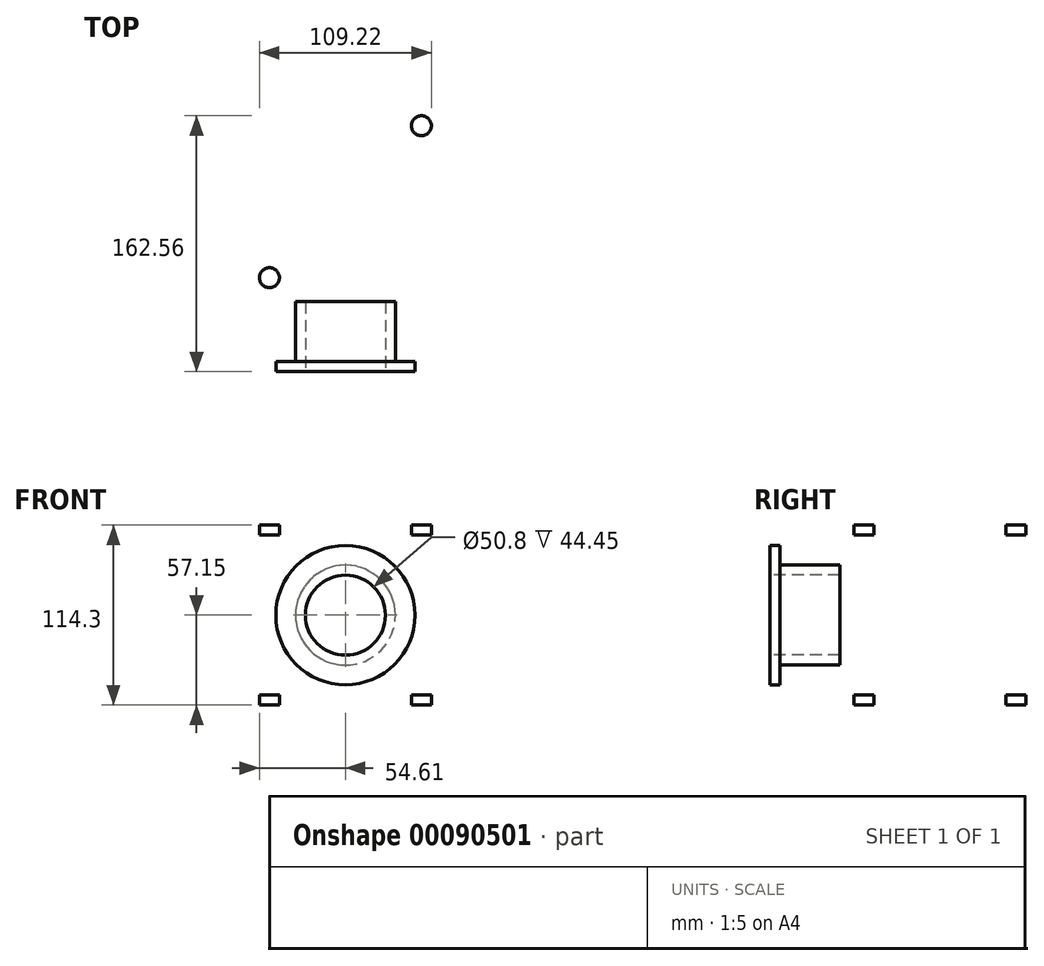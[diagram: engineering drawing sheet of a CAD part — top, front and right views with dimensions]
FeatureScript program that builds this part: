
annotation { "Feature Type Name" : "Feature", "Feature Type Description" : "" }
export const myFeature = defineFeature(function(context is Context, id is Id, definition is map)
    precondition{}
    {
        {
            var Q0;
            Q0=qCreatedBy(makeId("Top.planeOp"),FACE);
            var sketch = newSketch(context, id + "F0", { "sketchPlane" : qUnion([Q0])});
            skLineSegment(sketch, "E0", {"start": v(0, 63.5) * mm, "end": v(63.5, 63.5) * mm});
            skLineSegment(sketch, "E1", {"start": v(63.5, 63.5) * mm, "end": v(63.5, 0) * mm});
            skLineSegment(sketch, "E2.MirrorCS", {"start": v(-63.5, 63.5) * mm, "end": v(-63.5, 0) * mm});
            skLineSegment(sketch, "E3.MirrorCS", {"start": v(0, 63.5) * mm, "end": v(-63.5, 63.5) * mm});
            skLineSegment(sketch, "E4.MirrorCS", {"start": v(-63.5, -63.5) * mm, "end": v(-63.5, 0) * mm});
            skLineSegment(sketch, "E5.MirrorCS", {"start": v(0, -63.5) * mm, "end": v(-63.5, -63.5) * mm});
            skLineSegment(sketch, "E6.MirrorCS", {"start": v(0, -63.5) * mm, "end": v(63.5, -63.5) * mm});
            skLineSegment(sketch, "E7.MirrorCS", {"start": v(63.5, -63.5) * mm, "end": v(63.5, 0) * mm});
            skSolve(sketch);
        }
        {
            var Q0;
            Q0 = qSketchRegion(id + "F0", true);
            extrude(context, id + "F1", {"entities" : qUnion([Q0]), "depth" : 6.35 * mm});
        }
        {
            var Q0;
            Q0=makeQuery(id+"F1.opExtrude","SWEPT_EDGE",EDGE,{"disambiguationData":[OSD([sQuery(id+"F0.wireOp",EDGE,"E6.MirrorCS"),sQuery(id+"F0.wireOp",EDGE,"E7.MirrorCS")])]});
            var Q1;
            Q1=makeQuery(id+"F1.opExtrude","SWEPT_EDGE",EDGE,{"disambiguationData":[OSD([sQuery(id+"F0.wireOp",EDGE,"E0"),sQuery(id+"F0.wireOp",EDGE,"E1")])]});
            var Q2;
            Q2=makeQuery(id+"F1.opExtrude","SWEPT_EDGE",EDGE,{"disambiguationData":[OSD([sQuery(id+"F0.wireOp",EDGE,"E4.MirrorCS"),sQuery(id+"F0.wireOp",EDGE,"E5.MirrorCS")])]});
            var Q3;
            Q3=makeQuery(id+"F1.opExtrude","SWEPT_EDGE",EDGE,{"disambiguationData":[OSD([sQuery(id+"F0.wireOp",EDGE,"E2.MirrorCS"),sQuery(id+"F0.wireOp",EDGE,"E3.MirrorCS")])]});
            fillet(context, id + "F2", {"entities" : qUnion([Q0, Q1, Q2, Q3]), "radius" : 25.4 * mm, "tangentPropagation" : true, "allowEdgeOverflow" : false});
        }
        {
            var Q0;
            Q0=makeQuery(id+"F1.opExtrude","CAP_FACE",FACE,{"disambiguationData":[OSD([sQuery(id+"F0.wireOp",EDGE,"E0"),sQuery(id+"F0.wireOp",EDGE,"E1"),sQuery(id+"F0.wireOp",EDGE,"E2.MirrorCS"),sQuery(id+"F0.wireOp",EDGE,"E3.MirrorCS"),sQuery(id+"F0.wireOp",EDGE,"E4.MirrorCS"),sQuery(id+"F0.wireOp",EDGE,"E5.MirrorCS"),sQuery(id+"F0.wireOp",EDGE,"E6.MirrorCS"),sQuery(id+"F0.wireOp",EDGE,"E7.MirrorCS")])],"isStart":false});
            var sketch = newSketch(context, id + "F3", { "sketchPlane" : qUnion([Q0])});
            skCircle(sketch, "E8", {"center": v(0, 0) * mm, "radius": 47.63 * mm});
            skSolve(sketch);
        }
        {
            var Q0;
            Q0 = qSketchRegion(id + "F3", true);
            extrude(context, id + "F4", {"entities" : qUnion([Q0]), "operationType" : NewBodyOperationType.ADD, "depth" : 101.6 * mm});
        }
        {
            var Q0;
            Q0=makeQuery(id+"F4.opExtrude","CAP_FACE",FACE,{"disambiguationData":[OSD([sQuery(id+"F3.wireOp",EDGE,"E8")])],"isStart":false});
            var sketch = newSketch(context, id + "F5", { "sketchPlane" : qUnion([Q0])});
            skLineSegment(sketch, "E9", {"start": v(0, 63.5) * mm, "end": v(63.5, 63.5) * mm});
            skLineSegment(sketch, "E10", {"start": v(63.5, 63.5) * mm, "end": v(63.5, 0) * mm});
            skLineSegment(sketch, "E11.MirrorCS", {"start": v(0, 63.5) * mm, "end": v(-63.5, 63.5) * mm});
            skLineSegment(sketch, "E12.MirrorCS", {"start": v(-63.5, 63.5) * mm, "end": v(-63.5, 0) * mm});
            skLineSegment(sketch, "E13.MirrorCS", {"start": v(-63.5, -63.5) * mm, "end": v(-63.5, 0) * mm});
            skLineSegment(sketch, "E14.MirrorCS", {"start": v(0, -63.5) * mm, "end": v(-63.5, -63.5) * mm});
            skLineSegment(sketch, "E15.MirrorCS", {"start": v(0, -63.5) * mm, "end": v(63.5, -63.5) * mm});
            skLineSegment(sketch, "E16.MirrorCS", {"start": v(63.5, -63.5) * mm, "end": v(63.5, 0) * mm});
            skSolve(sketch);
        }
        {
            var Q0;
            Q0 = qSketchRegion(id + "F5", true);
            extrude(context, id + "F6", {"entities" : qUnion([Q0]), "operationType" : NewBodyOperationType.ADD, "depth" : 6.35 * mm});
        }
        {
            var Q0;
            Q0=makeQuery(id+"F6.opExtrude","SWEPT_EDGE",EDGE,{"disambiguationData":[OSD([sQuery(id+"F5.wireOp",EDGE,"E15.MirrorCS"),sQuery(id+"F5.wireOp",EDGE,"E16.MirrorCS")])]});
            var Q1;
            Q1=makeQuery(id+"F6.opExtrude","SWEPT_EDGE",EDGE,{"disambiguationData":[OSD([sQuery(id+"F5.wireOp",EDGE,"E13.MirrorCS"),sQuery(id+"F5.wireOp",EDGE,"E14.MirrorCS")])]});
            var Q2;
            Q2=makeQuery(id+"F6.opExtrude","SWEPT_EDGE",EDGE,{"disambiguationData":[OSD([sQuery(id+"F5.wireOp",EDGE,"E9"),sQuery(id+"F5.wireOp",EDGE,"E10")])]});
            var Q3;
            Q3=makeQuery(id+"F6.opExtrude","SWEPT_EDGE",EDGE,{"disambiguationData":[OSD([sQuery(id+"F5.wireOp",EDGE,"E11.MirrorCS"),sQuery(id+"F5.wireOp",EDGE,"E12.MirrorCS")])]});
            fillet(context, id + "F7", {"entities" : qUnion([Q0, Q1, Q2, Q3]), "radius" : 25.4 * mm, "tangentPropagation" : true, "allowEdgeOverflow" : false});
        }
        {
            var Q0;
            Q0=qCreatedBy(makeId("Front.planeOp"),FACE);
            var sketch = newSketch(context, id + "F8", { "sketchPlane" : qUnion([Q0])});
            skCircle(sketch, "E17", {"center": v(0, 57.15) * mm, "radius": 31.75 * mm});
            skSolve(sketch);
        }
        {
            var Q0;
            Q0 = qSketchRegion(id + "F8", true);
            extrude(context, id + "F9", {"entities" : qUnion([Q0]), "operationType" : NewBodyOperationType.ADD, "depth" : 101.6 * mm});
        }
        {
            var Q0;
            Q0=makeQuery(id+"F9.opExtrude","CAP_FACE",FACE,{"disambiguationData":[OSD([sQuery(id+"F8.wireOp",EDGE,"E17")])],"isStart":false});
            var sketch = newSketch(context, id + "F10", { "sketchPlane" : qUnion([Q0])});
            skCircle(sketch, "E18", {"center": v(0, 57.15) * mm, "radius": 44.2 * mm});
            skSolve(sketch);
        }
        {
            var Q0;
            Q0=makeQuery(id+"F10.imprint","IMPRINT",FACE,{"disambiguationData":[TD([[makeQuery(id+"F10.imprint","IMPRINT",EDGE,{"derivedFrom":sQuery(id+"F10.wireOp",EDGE,"E18")}),1.0]])]});
            var Q1;
            Q1=makeQuery(id+"F10.imprint","IMPRINT",FACE,{"disambiguationData":[TD([[makeQuery(id+"F10.imprint","IMPRINT",EDGE,{"derivedFrom":makeQuery(id+"F9.opExtrude","CAP_EDGE",EDGE,{"disambiguationData":[OSD([sQuery(id+"F8.wireOp",EDGE,"E17")])],"isStart":false})}),1.0]])]});
            extrude(context, id + "F11", {"entities" : qUnion([Q0, Q1]), "operationType" : NewBodyOperationType.ADD, "depth" : 6.35 * mm});
        }
        {
            var Q0;
            Q0=makeQuery(id+"F6.opExtrude","CAP_FACE",FACE,{"disambiguationData":[OSD([sQuery(id+"F5.wireOp",EDGE,"E9"),sQuery(id+"F5.wireOp",EDGE,"E10"),sQuery(id+"F5.wireOp",EDGE,"E11.MirrorCS"),sQuery(id+"F5.wireOp",EDGE,"E12.MirrorCS"),sQuery(id+"F5.wireOp",EDGE,"E13.MirrorCS"),sQuery(id+"F5.wireOp",EDGE,"E14.MirrorCS"),sQuery(id+"F5.wireOp",EDGE,"E15.MirrorCS"),sQuery(id+"F5.wireOp",EDGE,"E16.MirrorCS")])],"isStart":false});
            var sketch = newSketch(context, id + "F12", { "sketchPlane" : qUnion([Q0])});
            skCircle(sketch, "E19", {"center": v(0, 0) * mm, "radius": 38.1 * mm});
            skSolve(sketch);
        }
        {
            var Q0;
            Q0 = qSketchRegion(id + "F12", true);
            extrude(context, id + "F13", {"entities" : qUnion([Q0]), "operationType" : NewBodyOperationType.REMOVE, "oppositeDirection" : true, "depth" : 114.3 * mm});
        }
        {
            var Q0;
            Q0=makeQuery(id+"F11.opExtrude","CAP_FACE",FACE,{"disambiguationData":[OSD([sQuery(id+"F10.wireOp",EDGE,"E18")])],"isStart":false});
            var sketch = newSketch(context, id + "F14", { "sketchPlane" : qUnion([Q0])});
            skCircle(sketch, "E20", {"center": v(0, 57.15) * mm, "radius": 25.4 * mm});
            skSolve(sketch);
        }
        {
            var Q0;
            Q0=makeQuery(id+"F14.imprint","IMPRINT",FACE,{"disambiguationData":[TD([[makeQuery(id+"F14.imprint","IMPRINT",EDGE,{"derivedFrom":sQuery(id+"F14.wireOp",EDGE,"E20")}),1.0]])]});
            extrude(context, id + "F15", {"entities" : qUnion([Q0]), "operationType" : NewBodyOperationType.REMOVE, "oppositeDirection" : true, "depth" : 88.9 * mm});
        }
        {
            var Q0;
            Q0=makeQuery(id+"F6.opExtrude","CAP_FACE",FACE,{"disambiguationData":[OSD([sQuery(id+"F5.wireOp",EDGE,"E9"),sQuery(id+"F5.wireOp",EDGE,"E10"),sQuery(id+"F5.wireOp",EDGE,"E11.MirrorCS"),sQuery(id+"F5.wireOp",EDGE,"E12.MirrorCS"),sQuery(id+"F5.wireOp",EDGE,"E13.MirrorCS"),sQuery(id+"F5.wireOp",EDGE,"E14.MirrorCS"),sQuery(id+"F5.wireOp",EDGE,"E15.MirrorCS"),sQuery(id+"F5.wireOp",EDGE,"E16.MirrorCS")])],"isStart":false});
            var sketch = newSketch(context, id + "F16", { "sketchPlane" : qUnion([Q0])});
            skCircle(sketch, "E21", {"center": v(-48.26, 48.26) * mm, "radius": 6.35 * mm});
            skCircle(sketch, "E22.MirrorC", {"center": v(48.26, 48.26) * mm, "radius": 6.35 * mm});
            skCircle(sketch, "E23.MirrorC", {"center": v(-48.26, -48.26) * mm, "radius": 6.35 * mm});
            skCircle(sketch, "E24.MirrorC", {"center": v(48.26, -48.26) * mm, "radius": 6.35 * mm});
            skSolve(sketch);
        }
        {
            var Q0;
            Q0=makeQuery(id+"F16.imprint","IMPRINT",FACE,{"disambiguationData":[TD([[makeQuery(id+"F16.imprint","IMPRINT",EDGE,{"derivedFrom":sQuery(id+"F16.wireOp",EDGE,"E21")}),1.0]])]});
            var Q1;
            Q1=makeQuery(id+"F16.imprint","IMPRINT",FACE,{"disambiguationData":[TD([[makeQuery(id+"F16.imprint","IMPRINT",EDGE,{"derivedFrom":sQuery(id+"F16.wireOp",EDGE,"E22.MirrorC")}),-1.0]])]});
            var Q2;
            Q2=makeQuery(id+"F16.imprint","IMPRINT",FACE,{"disambiguationData":[TD([[makeQuery(id+"F16.imprint","IMPRINT",EDGE,{"derivedFrom":sQuery(id+"F16.wireOp",EDGE,"E24.MirrorC")}),1.0]])]});
            var Q3;
            Q3=makeQuery(id+"F16.imprint","IMPRINT",FACE,{"disambiguationData":[TD([[makeQuery(id+"F16.imprint","IMPRINT",EDGE,{"derivedFrom":sQuery(id+"F16.wireOp",EDGE,"E23.MirrorC")}),-1.0]])]});
            extrude(context, id + "F17", {"entities" : qUnion([Q0, Q1, Q2, Q3]), "operationType" : NewBodyOperationType.REMOVE, "oppositeDirection" : true, "depth" : 114.3 * mm});
        }
    });
